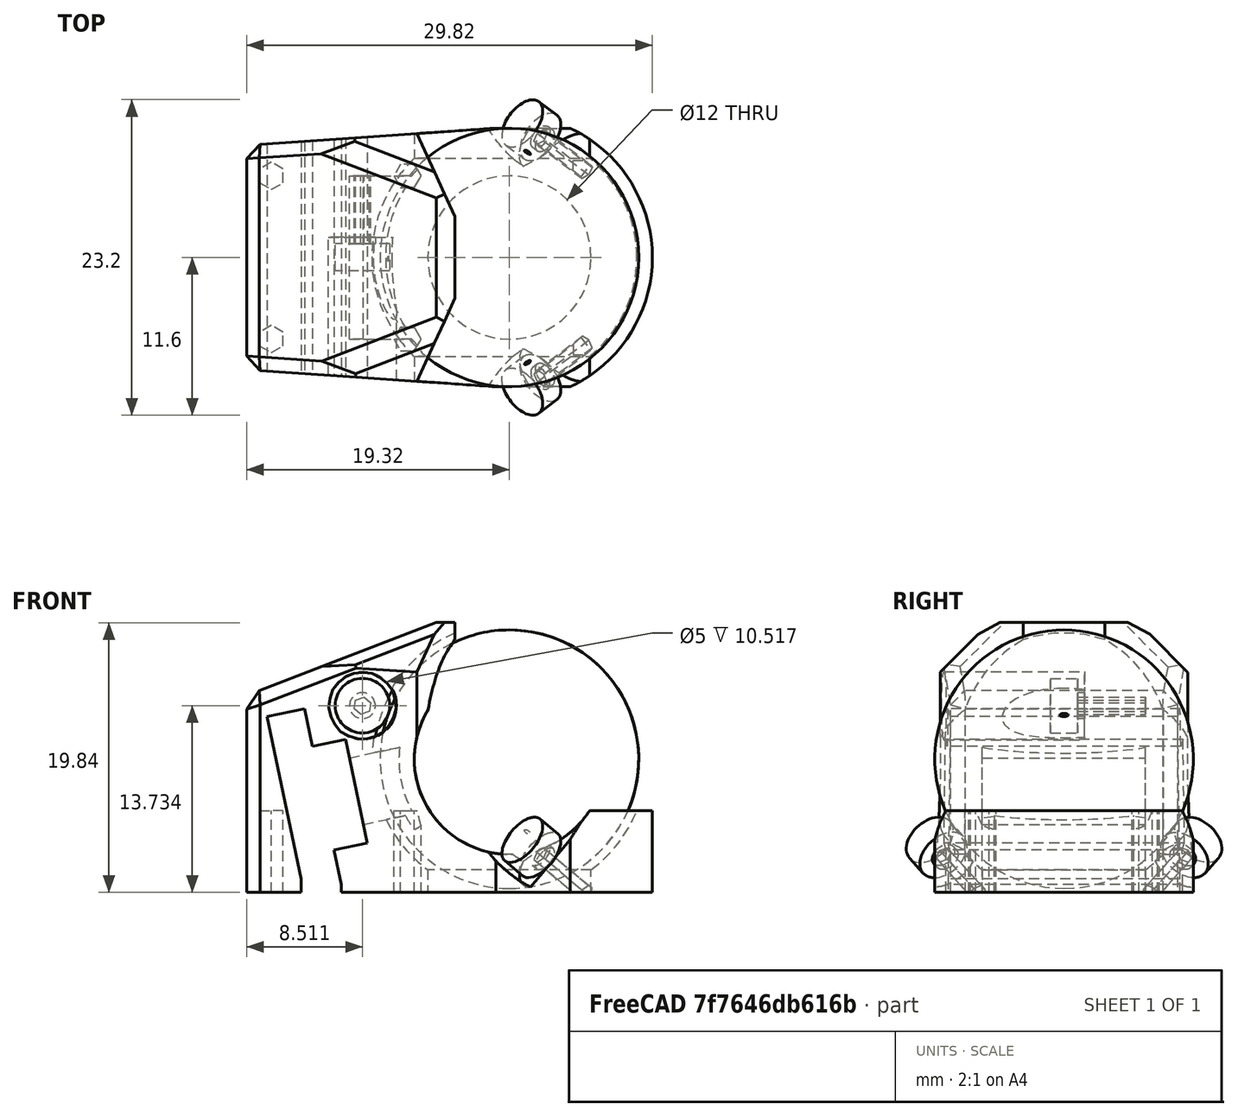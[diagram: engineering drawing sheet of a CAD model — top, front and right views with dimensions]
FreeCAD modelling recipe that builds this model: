
FCSTD DOCUMENT  (FreeCAD 0.21R33771 (Git))
Label: trackball-case-19mm
License: All rights reserved
LicenseURL: http://en.wikipedia.org/wiki/All_rights_reserved
objects: Sketcher::SketchObject×16, PartDesign::Pocket×11, PartDesign::Pad×3, PartDesign::Line×2, PartDesign::PolarPattern×2, PartDesign::Body×2, Spreadsheet::Sheet×1, PartDesign::AdditiveSphere×1, PartDesign::Point×1, PartDesign::Plane×1, PartDesign::SubtractiveSphere×1, PartDesign::Mirrored×1, PartDesign::Chamfer×1
note: 59 computed .brp shape members not serialized (recipe doc carries the construction recipe); baked Part::Feature solids carry a one-line shape summary decoded from their .brp

FEATURE [Sketcher::SketchObject] Sketch
  FullyConstrained = false
  MapMode = 5
  Placement = pos=(0,0,0) rot=(1,0,0;1.5708rad)
  Support = -> [XZ_Plane]
  expr: Constraints[18] = Spreadsheet.radius + 2
  expr: Constraints[1] = Spreadsheet.radius * 2
  expr: Constraints[2] = Spreadsheet.ball_z
  expr: Constraints[35] = 2 * (Spreadsheet.radius + Spreadsheet.clearance)
  expr: Constraints[40] = Spreadsheet.radius * 2 - 0.6
  expr: Constraints[86] = Spreadsheet.radius + Spreadsheet.clearance + 1.2
  expr: Constraints[91] = Spreadsheet.radius + 1
  sketch-geometry (32):
    g0: Circle CenterX=0 CenterY=9.8 CenterZ=0 NormalX=0 NormalY=0 NormalZ=1 AngleXU=0 Radius=9.5025
    g1: LineSegment StartX=0 StartY=9.8 StartZ=0 EndX=-23.9742 EndY=4.78934 EndZ=0
    g2: LineSegment StartX=-12.6299 StartY=14.0051 StartZ=0 EndX=-17.8178 EndY=12.9208 EndZ=0
    g3: LineSegment StartX=-17.8178 StartY=12.9208 StartZ=0 EndX=-15.1173 EndY=0 EndZ=0
    g4: LineSegment StartX=-15.1173 StartY=0 StartZ=0 EndX=-9.92944 EndY=1.08428 EndZ=0
    g5: LineSegment StartX=-9.92944 StartY=1.08428 StartZ=0 EndX=-12.6299 EndY=14.0051 EndZ=0
    g6: LineSegment StartX=-9.92944 StartY=1.08428 StartZ=0 EndX=-11.2592 EndY=7.4468 EndZ=0
    g7: LineSegment StartX=10.5025 StartY=10 StartZ=0 EndX=10.5025 EndY=0 EndZ=0
    g8: LineSegment StartX=10.5025 StartY=6 StartZ=0 EndX=0 EndY=6 EndZ=0
    g9: LineSegment StartX=0 StartY=6 StartZ=0 EndX=-3.31715 EndY=19.3424 EndZ=0
    g10: LineSegment StartX=-3.31715 StartY=19.3424 StartZ=0 EndX=-19.3178 EndY=19.3424 EndZ=0
    g11: LineSegment StartX=-19.3178 StartY=19.3424 StartZ=0 EndX=-19.3178 EndY=0 EndZ=0
    g12: LineSegment StartX=-19.3178 StartY=0 StartZ=0 EndX=10.5025 EndY=0 EndZ=0
    g13: LineSegment StartX=10.5025 StartY=0 StartZ=0 EndX=10.5025 EndY=6 EndZ=0
    g14: Circle CenterX=0 CenterY=9.8 CenterZ=0 NormalX=0 NormalY=0 NormalZ=1 AngleXU=0 Radius=10.1025
    g15: LineSegment StartX=0 StartY=6 StartZ=0 EndX=9.36058 EndY=6 EndZ=0
    g16: LineSegment StartX=-3.44146 StartY=19.8424 StartZ=0 EndX=-3.31715 EndY=19.3424 EndZ=0
    g17: LineSegment StartX=-15.077 StartY=13.4936 StartZ=0 EndX=-17.8178 EndY=12.9208 EndZ=0
    g18: LineSegment StartX=-17.8178 StartY=12.9208 StartZ=0 EndX=-15.3263 EndY=1 EndZ=0
    g19: LineSegment StartX=-15.3263 StartY=1 StartZ=0 EndX=-15.3263 EndY=0 EndZ=0
    g20: LineSegment StartX=-15.3263 StartY=0 StartZ=0 EndX=-19.3178 EndY=0 EndZ=0
    g21: LineSegment StartX=-15.077 StartY=13.4936 StartZ=0 EndX=-14.5042 EndY=10.7529 EndZ=0
    g22: LineSegment StartX=-14.5042 StartY=10.7529 StartZ=0 EndX=-12.0571 EndY=11.2643 EndZ=0
    g23: LineSegment StartX=-12.0571 StartY=11.2643 StartZ=0 EndX=-10.4613 EndY=3.62929 EndZ=0
    g24: LineSegment StartX=-10.4613 StartY=3.62929 StartZ=0 EndX=-12.9085 EndY=3.11784 EndZ=0
    g25: LineSegment StartX=-12.9085 StartY=3.11784 StartZ=0 EndX=-12.3766 EndY=0.572828 EndZ=0
    g26: LineSegment StartX=-12.3766 StartY=0.572828 StartZ=0 EndX=-12.3766 EndY=0 EndZ=0
    g27: LineSegment StartX=-12.3766 StartY=0 StartZ=0 EndX=10.5025 EndY=0 EndZ=0
    g28: LineSegment StartX=-15.077 StartY=13.4936 StartZ=0 EndX=-12.3766 EndY=0.572828 EndZ=0
    g29: LineSegment StartX=-19.3178 StartY=0 StartZ=0 EndX=-19.3178 EndY=14.4871 EndZ=0
    g30: LineSegment StartX=-19.3178 StartY=14.4871 StartZ=0 EndX=-5.37659 EndY=19.8424 EndZ=0
    g31: LineSegment StartX=-5.37659 StartY=19.8424 StartZ=0 EndX=-3.44146 EndY=19.8424 EndZ=0
  constraints (92):
    c: PointOnObject(g0,g-2)
    c: Diameter(g0) = 19.005
    c: Distance(g0,g-1) = 9.8
    c: Coincident(g1,g0)
    c: Coincident(g3,g2)
    c: Coincident(g4,g3)
    c: Coincident(g5,g4)
    c: Coincident(g5,g2)
    c: Perpendicular(g1,g5)
    c: Perpendicular(g1,g3)
    c: Parallel(g2,g1)
    c: Parallel(g4,g1)
    c: Distance(g3,g1) = 6.5
    c: Distance(g2,g1) = 6.7
    c: Distance(g4) = 5.3
    c: Coincident(g6,g4)
    c: PointOnObject(g6,g1)
    c: PointOnObject(g6,g5)
    c: Distance(g6,g0) = 11.5025
    c: PointOnObject(g7,g-1)
    c: Vertical(g7)
    c: PointOnObject(g8,g7)
    c: PointOnObject(g8,g-2)
    c: Horizontal(g8)
    c: Coincident(g9,g8)
    c: Coincident(g10,g9)
    c: Horizontal(g10)
    c: Coincident(g11,g10)
    c: PointOnObject(g11,g-1)
    c: Vertical(g11)
    c: Coincident(g12,g11)
    c: Coincident(g12,g7)
    c: Coincident(g13,g12)
    c: Coincident(g13,g8)
    c: Coincident(g14,g0)
    c: Diameter(g14) = 20.205
    c: PointOnObject(g9,g14)
    c: Coincident(g15,g8)
    c: PointOnObject(g15,g8)
    c: PointOnObject(g15,g14)
    c: Distance(g9,g15) = 18.405
    c: Coincident(g16,g9)
    c: Parallel(g16,g9)
    c: Distance(g2,g11) = 1.5
    c: PointOnObject(g3,g12)
    c: PointOnObject(g17,g2)
    c: Coincident(g17,g2)
    c: Coincident(g18,g17)
    c: PointOnObject(g18,g3)
    c: Coincident(g19,g18)
    c: PointOnObject(g19,g12)
    c: Vertical(g19)
    c: Coincident(g20,g19)
    c: Coincident(g20,g11)
    c: Coincident(g21,g17)
    c: Coincident(g22,g21)
    c: PointOnObject(g22,g5)
    c: Coincident(g23,g22)
    c: PointOnObject(g23,g5)
    c: Coincident(g24,g23)
    c: Coincident(g25,g24)
    c: PointOnObject(g25,g4)
    c: Coincident(g26,g25)
    c: PointOnObject(g26,g12)
    c: Vertical(g26)
    c: Coincident(g27,g26)
    c: Coincident(g27,g13)
    c: Coincident(g28,g17)
    c: Coincident(g28,g25)
    c: PointOnObject(g21,g28)
    c: PointOnObject(g24,g28)
    c: Perpendicular(g22,g21)
    c: Perpendicular(g25,g24)
    c: Distance(g22,g1) = 3.9
    c: Distance(g23,g1) = 3.9
    c: Distance(g22) = 2.5
    c: Perpendicular(g1,g28)
    c: Distance(g19) = 1
    c: Coincident(g29,g20)
    c: PointOnObject(g29,g11)
    c: Coincident(g30,g29)
    c: Coincident(g31,g30)
    c: Coincident(g31,g16)
    c: Horizontal(g31)
    c: Distance(g16,g10) = 0.5
    c: Distance(g17,g30) = 2
    c: Distance(g0,g30) = 11.3025
    c: Distance(g15,g8) = 1.14192
    c: Distance(g16,g27) = 19.8424
    c: Distance(g20,g-2) = 19.3178
    c: Distance(g13) = 6
    c: Distance(g8,g13) = 10.5025
FEATURE [Spreadsheet::Sheet] Spreadsheet
  cells = A1='radius; B1(radius)=9.5025; A2='ball_z; B2(ball_z)=9.8; A3='ball_clearance; B3(clearance)=0.6; A4='bearing_radius; B4(bearing_radius)=2; A5='bearing_t; B5(bearing_t)=2; A6='bearing_a1; B6(bearing_a1)=110; A7='bearing_a2; B7(bearing_a2)=30
FEATURE [PartDesign::Pad] Pad
  Direction = (0,-1,-2e-16)
  Length = 19.005
  Length2 = 10
  Midplane = true
  Placement = pos=(0,0,0) rot=(1,0,0;1.5708rad)
  Profile = -> Sketch
  ReferenceAxis = -> Sketch [N_Axis]
  Type = 0
  expr: Length = Spreadsheet.radius * 2
FEATURE [PartDesign::AdditiveSphere] Sphere001
  Angle1 = -90
  Angle2 = 90
  Angle3 = 360
  AttacherType = Attacher::AttachEngine3D
  AttachmentOffset = pos=(0,0,9.8) rot=(0,0,1;0rad)
  MapMode = 5
  Placement = pos=(0,0,9.8) rot=(0,0,1;0rad)
  Radius = 9.5025
  Support = -> [XY_Plane001]
  expr: .AttachmentOffset.Base.z = Spreadsheet.ball_z
  expr: Radius = Spreadsheet.radius
FEATURE [Sketcher::SketchObject] Sketch001
  FullyConstrained = true
  MapMode = 5
  Placement = pos=(0,0,0) rot=(1,0,0;1.5708rad)
  Support = -> [XZ_Plane]
  expr: Constraints[1] = Spreadsheet.ball_z
  expr: Constraints[2] = 7 * 2
  sketch-geometry (1):
    g0: Circle CenterX=0 CenterY=9.8 CenterZ=0 NormalX=0 NormalY=0 NormalZ=1 AngleXU=0 Radius=7
  constraints (3):
    c: PointOnObject(g0,g-2)
    c: Distance(g0,g-1) = 9.8
    c: Diameter(g0) = 14
FEATURE [Sketcher::SketchObject] Sketch002
  FullyConstrained = true
  MapMode = 5
  Support = -> [XY_Plane]
  sketch-geometry (1):
    g0: Circle CenterX=0 CenterY=0 CenterZ=0 NormalX=0 NormalY=0 NormalZ=1 AngleXU=0 Radius=6
  constraints (2):
    c: Coincident(g0,g-1)
    c: Diameter(g0) = 12
FEATURE [Sketcher::SketchObject] Sketch006
  FullyConstrained = false
  MapMode = 5
  Placement = pos=(0,0,0) rot=(1,0,0;1.5708rad)
  Support = -> [XZ_Plane]
  expr: Constraints[1] = Spreadsheet.ball_z
  expr: Constraints[2] = Spreadsheet.bearing_a1
  expr: Constraints[3] = Spreadsheet.bearing_a2
  expr: Constraints[5] = (Spreadsheet.bearing_a1 + Spreadsheet.bearing_a2) / 2
  sketch-geometry (3):
    g0: LineSegment StartX=0 StartY=9.8 StartZ=0 EndX=-24.3543 EndY=18.6642 EndZ=0
    g1: LineSegment StartX=-0.855559 StartY=12.664 StartZ=0 EndX=7.91392 EndY=-2.52517 EndZ=0
    g2: LineSegment StartX=7.70104 StartY=18.9777 StartZ=0 EndX=-6.79818 EndY=1.69825 EndZ=0
  constraints (6):
    c: PointOnObject(g0,g-2)
    c: Distance(g0,g-1) = 9.8
    c: Angle(g0,g-2) = 1.91986
    c: Angle(g-2,g1) = 0.523599
    c: PointOnObject(g0,g2)
    c: Angle(g0,g2) = 1.22173
FEATURE [PartDesign::Line] DatumLine
  AttacherType = Attacher::AttachEngineLine
  Length = 20
  MapMode = 29
  Placement = pos=(-4.82556,-9e-16,4.04912) rot=(-0.684791,0.684791,0.249244;3.63013rad)
  ResizeMode = 0
  Support = -> [Sketch006]
FEATURE [PartDesign::Point] DatumPoint
  AttacherType = Attacher::AttachEnginePoint
  AttachmentOffset = pos=(0,0,9.8) rot=(0,0,1;0rad)
  MapMode = 41
  Placement = pos=(0,0,9.8) rot=(0,0,1;0rad)
  Support = -> [X_Axis,Y_Axis]
  expr: .AttachmentOffset.Base.z = Spreadsheet.ball_z
FEATURE [PartDesign::Plane] DatumPlane
  AttachmentOffset = pos=(0,0,0) rot=(0.654654,0.377964,-0.654654;2.41886rad)
  Length = 85.316
  MapMode = 7
  Placement = pos=(1.8e-15,-3.4e-15,9.8) rot=(0.11982,0.958967,-0.256954;2.30059rad)
  ResizeMode = 0
  Support = -> [DatumLine,DatumPoint]
  Width = 93.3965
FEATURE [Sketcher::SketchObject] Sketch003
  FullyConstrained = true
  MapMode = 5
  Placement = pos=(9e-16,-3.6e-15,9.8) rot=(0.11982,0.958967,-0.256954;2.30059rad)
  Support = -> [DatumPlane]
  expr: Constraints[0] = Spreadsheet.bearing_radius * 2
  expr: Constraints[2] = Spreadsheet.radius + Spreadsheet.bearing_radius
  expr: Constraints[4] = (Spreadsheet.bearing_radius + 0.5) * 2
  expr: Constraints[6] = (Spreadsheet.bearing_a1 + Spreadsheet.bearing_a2) / 2
  sketch-geometry (3):
    g0: Circle CenterX=3.93409 CenterY=10.8088 CenterZ=0 NormalX=0 NormalY=0 NormalZ=1 AngleXU=0 Radius=2
    g1: LineSegment StartX=0 StartY=0 StartZ=0 EndX=3.93409 EndY=10.8088 EndZ=0
    g2: Circle CenterX=3.93409 CenterY=10.8088 CenterZ=0 NormalX=0 NormalY=0 NormalZ=1 AngleXU=0 Radius=2.5
  constraints (7):
    c: Diameter(g0) = 4
    c: Coincident(g1,g0)
    c: Distance(g1) = 11.5025
    c: Coincident(g2,g0)
    c: Diameter(g2) = 5
    c: Coincident(g1,g-1)
    c: Angle(g-1,g1) = 1.22173
FEATURE [Sketcher::SketchObject] Sketch004
  AttachmentOffset = pos=(0,0,1) rot=(0,0,1;0rad)
  FullyConstrained = true
  MapMode = 5
  Placement = pos=(0.663414,-0.5,9.24333) rot=(0.11982,0.958967,-0.256954;2.30059rad)
  Support = -> [DatumPlane]
  expr: .AttachmentOffset.Base.z = Spreadsheet.bearing_t / 2
  expr: Constraints[0] = Spreadsheet.bearing_radius * 2
  expr: Constraints[2] = Spreadsheet.radius + Spreadsheet.bearing_radius
  expr: Constraints[6] = (Spreadsheet.bearing_a1 + Spreadsheet.bearing_a2) / 2
  sketch-geometry (3):
    g0: Circle CenterX=3.93409 CenterY=10.8088 CenterZ=0 NormalX=0 NormalY=0 NormalZ=1 AngleXU=0 Radius=2
    g1: LineSegment StartX=0 StartY=0 StartZ=0 EndX=3.93409 EndY=10.8088 EndZ=0
    g2: Circle CenterX=3.93409 CenterY=10.8088 CenterZ=0 NormalX=0 NormalY=0 NormalZ=1 AngleXU=0 Radius=0.95
  constraints (7):
    c: Diameter(g0) = 4
    c: Coincident(g1,g0)
    c: Distance(g1) = 11.5025
    c: Coincident(g2,g0)
    c: Diameter(g2) = 1.9
    c: Coincident(g1,g-1)
    c: Angle(g-1,g1) = 1.22173
FEATURE [Sketcher::SketchObject] Sketch005
  AttachmentOffset = pos=(0,0,1) rot=(0,0,1;0rad)
  FullyConstrained = true
  MapMode = 5
  Placement = pos=(0.663414,-0.5,9.24333) rot=(0.11982,0.958967,-0.256954;2.30059rad)
  Support = -> [DatumPlane]
  expr: .AttachmentOffset.Base.z = Spreadsheet.bearing_t / 2
  expr: Constraints[0] = Spreadsheet.bearing_radius * 2
  expr: Constraints[29] = (Spreadsheet.bearing_a1 + Spreadsheet.bearing_a2) / 2
  expr: Constraints[2] = Spreadsheet.radius + Spreadsheet.bearing_radius
  sketch-geometry (11):
    g0: Circle CenterX=3.93409 CenterY=10.8088 CenterZ=0 NormalX=0 NormalY=0 NormalZ=1 AngleXU=0 Radius=2
    g1: LineSegment StartX=0 StartY=0 StartZ=0 EndX=3.93409 EndY=10.8088 EndZ=0
    g2: LineSegment StartX=3.93409 StartY=10.8088 StartZ=0 EndX=3.93409 EndY=12.8088 EndZ=0
    g3: Circle CenterX=3.93409 CenterY=10.8088 CenterZ=0 NormalX=0 NormalY=0 NormalZ=1 AngleXU=0 Radius=0.65
    g4: LineSegment StartX=3.93409 StartY=11.4588 StartZ=0 EndX=3.37117 EndY=11.1338 EndZ=0
    g5: LineSegment StartX=3.37117 StartY=11.1338 StartZ=0 EndX=3.37117 EndY=10.4838 EndZ=0
    g6: LineSegment StartX=3.37117 StartY=10.4838 StartZ=0 EndX=3.93409 EndY=10.1588 EndZ=0
    g7: LineSegment StartX=3.93409 StartY=10.1588 StartZ=0 EndX=4.497 EndY=10.4838 EndZ=0
    g8: LineSegment StartX=4.497 StartY=10.4838 StartZ=0 EndX=4.497 EndY=11.1338 EndZ=0
    g9: LineSegment StartX=4.497 StartY=11.1338 StartZ=0 EndX=3.93409 EndY=11.4588 EndZ=0
    g10: Circle CenterX=3.93409 CenterY=10.8088 CenterZ=0 NormalX=0 NormalY=0 NormalZ=1 AngleXU=0 Radius=0.65
  constraints (26):
    c: Diameter(g0) = 4
    c: Coincident(g1,g0)
    c: Distance(g1) = 11.5025
    c: Coincident(g2,g0)
    c: PointOnObject(g2,g0)
    c: Vertical(g2)
    c: Coincident(g3,g0)
    c: Diameter(g3) = 1.3
    c: Coincident(g4,g5)
    c: Coincident(g5,g6)
    c: Coincident(g6,g7)
    c: Coincident(g7,g8)
    c: Coincident(g8,g9)
    c: Coincident(g9,g4)
    c: Equal(g4, g5-g9) x5
    c: PointOnObject(g4,g10)
    c: PointOnObject(g5,g10)
    c: PointOnObject(g6,g10)
    c: PointOnObject(g7,g10)
    c: PointOnObject(g8,g10)
    c: PointOnObject(g9,g10)
    c: Coincident(g10,g0)
    c: PointOnObject(g9,g3)
    c: PointOnObject(g4,g2)
    c: Coincident(g1,g-1)
    c: Angle(g-1,g1) = 1.22173
FEATURE [Sketcher::SketchObject] Sketch007
  FullyConstrained = true
  MapMode = 5
  Support = -> [XY_Plane]
  expr: Constraints[6] = Spreadsheet.radius + 1
  expr: Constraints[7] = Spreadsheet.radius * 2
  sketch-geometry (4):
    g0: ArcOfCircle CenterX=0 CenterY=0 CenterZ=0 NormalX=0 NormalY=0 NormalZ=1 AngleXU=0 Radius=10.5025 StartAngle=4.71239 EndAngle=7.85398
    g1: ArcOfCircle CenterX=0 CenterY=0 CenterZ=0 NormalX=0 NormalY=0 NormalZ=1 AngleXU=0 Radius=19.005 StartAngle=4.71239 EndAngle=7.85398
    g2: LineSegment StartX=0 StartY=19.005 StartZ=0 EndX=0 EndY=10.5025 EndZ=0
    g3: LineSegment StartX=0 StartY=-10.5025 StartZ=0 EndX=-3.5e-15 EndY=-19.005 EndZ=0
  constraints (12):
    c: Coincident(g0,g-1)
    c: PointOnObject(g0,g-2)
    c: PointOnObject(g0,g-2)
    c: Coincident(g1,g0)
    c: PointOnObject(g1,g-2)
    c: PointOnObject(g1,g-2)
    c: Radius(g0) = 10.5025
    c: Radius(g1) = 19.005
    c: Coincident(g2,g1)
    c: Coincident(g2,g0)
    c: Coincident(g3,g0)
    c: Coincident(g3,g1)
FEATURE [Sketcher::SketchObject] Sketch008
  FullyConstrained = true
  MapMode = 5
  Support = -> [XY_Plane]
  expr: Constraints[10] = Spreadsheet.radius * 2
  expr: Constraints[33] = Spreadsheet.radius * 2
  expr: Constraints[34] = Spreadsheet.radius * 2
  expr: Constraints[36] = Spreadsheet.radius * 2
  sketch-geometry (14):
    g0: LineSegment StartX=-23 StartY=-9.5025 StartZ=0 EndX=-23 EndY=9.5025 EndZ=0
    g1: LineSegment StartX=-23 StartY=9.5025 StartZ=0 EndX=0 EndY=9.5025 EndZ=0
    g2: LineSegment StartX=0 StartY=9.5025 StartZ=0 EndX=0 EndY=-9.5025 EndZ=0
    g3: LineSegment StartX=0 StartY=-9.5025 StartZ=0 EndX=-23 EndY=-9.5025 EndZ=0
    g4: GeomPoint X=-11.5 Y=0 Z=0
    g5: LineSegment StartX=-23 StartY=8 StartZ=0 EndX=-1 EndY=9.5025 EndZ=0
    g6: LineSegment StartX=-1 StartY=9.5025 StartZ=0 EndX=-1 EndY=-9.5025 EndZ=0
    g7: LineSegment StartX=-1 StartY=-9.5025 StartZ=0 EndX=-23 EndY=-8 EndZ=0
    g8: LineSegment StartX=-1 StartY=-9.5025 StartZ=0 EndX=-1 EndY=-19.005 EndZ=0
    g9: LineSegment StartX=-1 StartY=-19.005 StartZ=0 EndX=-20.005 EndY=-19.005 EndZ=0
    g10: LineSegment StartX=-20.005 StartY=-19.005 StartZ=0 EndX=-20.005 EndY=19.005 EndZ=0
    g11: LineSegment StartX=-20.005 StartY=19.005 StartZ=0 EndX=-1 EndY=19.005 EndZ=0
    g12: LineSegment StartX=-1 StartY=19.005 StartZ=0 EndX=-1 EndY=9.5025 EndZ=0
    g13: LineSegment StartX=-23 StartY=8 StartZ=0 EndX=-23 EndY=-8 EndZ=0
  constraints (39):
    c: Coincident(g0,g1)
    c: Coincident(g1,g2)
    c: Coincident(g2,g3)
    c: Coincident(g3,g0)
    c: Horizontal(g1)
    c: Horizontal(g3)
    c: Vertical(g0)
    c: Vertical(g2)
    c: Symmetric(g1,g0,g4)
    c: PointOnObject(g4,g-1)
    c: Distance(g0) = 19.005
    c: PointOnObject(g1,g-2)
    c: Distance(g-1,g0) = 23
    c: PointOnObject(g5,g0)
    c: PointOnObject(g5,g1)
    c: Coincident(g6,g5)
    c: PointOnObject(g6,g3)
    c: Vertical(g6)
    c: Coincident(g7,g6)
    c: PointOnObject(g7,g0)
    c: Distance(g5,g-1) = 8
    c: Distance(g7,g-1) = 8
    c: Coincident(g8,g7)
    c: Vertical(g8)
    c: Coincident(g9,g8)
    c: Horizontal(g9)
    c: Coincident(g10,g9)
    c: Vertical(g10)
    c: Coincident(g11,g10)
    c: Horizontal(g11)
    c: Coincident(g12,g11)
    c: Coincident(g12,g5)
    c: Vertical(g12)
    c: Distance(g10,g-1) = 19.005
    c: Distance(g9,g-1) = 19.005
    c: Distance(g7,g-2) = 1
    c: Distance(g9) = 19.005
    c: Coincident(g13,g5)
    c: Coincident(g13,g7)
FEATURE [Sketcher::SketchObject] Sketch009
  FullyConstrained = false
  MapMode = 5
  Placement = pos=(0,0,0) rot=(1,0,0;1.5708rad)
  Support = -> [XZ_Plane]
  expr: Constraints[18] = Spreadsheet.radius + 2
  expr: Constraints[1] = Spreadsheet.radius * 2
  expr: Constraints[24] = 2 * (Spreadsheet.radius + Spreadsheet.clearance)
  expr: Constraints[2] = Spreadsheet.ball_z
  expr: Constraints[37] = Spreadsheet.radius + 3
  sketch-geometry (14):
    g0: Circle CenterX=0 CenterY=9.8 CenterZ=0 NormalX=0 NormalY=0 NormalZ=1 AngleXU=0 Radius=9.5025
    g1: LineSegment StartX=0 StartY=9.8 StartZ=0 EndX=-24.0621 EndY=4.77097 EndZ=0
    g2: LineSegment StartX=-12.6299 StartY=14.0051 StartZ=0 EndX=-17.8178 EndY=12.9208 EndZ=0
    g3: LineSegment StartX=-17.8178 StartY=12.9208 StartZ=0 EndX=-15.1173 EndY=0 EndZ=0
    g4: LineSegment StartX=-15.1173 StartY=0 StartZ=0 EndX=-9.92944 EndY=1.08428 EndZ=0
    g5: LineSegment StartX=-9.92944 StartY=1.08428 StartZ=0 EndX=-12.6299 EndY=14.0051 EndZ=0
    g6: LineSegment StartX=-9.92944 StartY=1.08428 StartZ=0 EndX=-11.2592 EndY=7.4468 EndZ=0
    g7: LineSegment StartX=-4.65284 StartY=18.7672 StartZ=0 EndX=-19.0178 EndY=18.7672 EndZ=0
    g8: LineSegment StartX=-19.0178 StartY=18.7672 StartZ=0 EndX=-19.0178 EndY=0 EndZ=0
    g9: Circle CenterX=0 CenterY=9.8 CenterZ=0 NormalX=0 NormalY=0 NormalZ=1 AngleXU=0 Radius=10.1025
    g10: LineSegment StartX=-12.7495 StartY=9.68935 StartZ=0 EndX=-11.7266 EndY=4.7951 EndZ=0
    g11: LineSegment StartX=-11.7266 StartY=4.7951 StartZ=0 EndX=0.511453 EndY=7.35288 EndZ=0
    g12: LineSegment StartX=-12.7495 StartY=9.68935 StartZ=0 EndX=-0.511453 EndY=12.2471 EndZ=0
    g13: LineSegment StartX=-0.511453 StartY=12.2471 StartZ=0 EndX=0.511453 EndY=7.35288 EndZ=0
  constraints (40):
    c: PointOnObject(g0,g-2)
    c: Diameter(g0) = 19.005
    c: Distance(g0,g-1) = 9.8
    c: Coincident(g1,g0)
    c: Coincident(g3,g2)
    c: Coincident(g4,g3)
    c: Coincident(g5,g4)
    c: Coincident(g5,g2)
    c: Perpendicular(g1,g5)
    c: Perpendicular(g1,g3)
    c: Parallel(g2,g1)
    c: Parallel(g4,g1)
    c: Distance(g3,g1) = 6.5
    c: Distance(g2,g1) = 6.7
    c: Distance(g4) = 5.3
    c: Coincident(g6,g4)
    c: PointOnObject(g6,g1)
    c: PointOnObject(g6,g5)
    c: Distance(g6,g0) = 11.5025
    c: Horizontal(g7)
    c: Coincident(g8,g7)
    c: PointOnObject(g8,g-1)
    c: Vertical(g8)
    c: Coincident(g9,g0)
    c: Diameter(g9) = 20.205
    c: PointOnObject(g7,g9)
    c: Distance(g2,g8) = 1.2
    c: PointOnObject(g3,g-1)
    c: Coincident(g11,g10)
    c: Coincident(g12,g10)
    c: Coincident(g13,g12)
    c: Coincident(g13,g11)
    c: Perpendicular(g1,g10)
    c: Perpendicular(g1,g13)
    c: Perpendicular(g13,g11)
    c: Perpendicular(g13,g12)
    c: PointOnObject(g0,g13)
    c: Distance(g0,g10) = 12.5025
    c: Distance(g10,g1) = 2.5
    c: Distance(g10,g1) = 2.5
FEATURE [PartDesign::Pocket] Pocket006  label="センサービューポート"
  BaseFeature = -> Pad
  Direction = (0,1,2e-16)
  Length = 12
  Length2 = 5
  Midplane = true
  Placement = pos=(0,0,0) rot=(1,0,0;1.5708rad)
  Profile = -> Sketch009
  ReferenceAxis = -> Sketch009 [N_Axis]
  Type = 0
FEATURE [PartDesign::SubtractiveSphere] Sphere
  Angle1 = -90
  Angle2 = 90
  Angle3 = 360
  AttacherType = Attacher::AttachEngine3D
  AttachmentOffset = pos=(0,0,9.8) rot=(0,0,1;0rad)
  BaseFeature = -> Pocket006
  MapMode = 5
  Placement = pos=(0,0,9.8) rot=(0,0,1;0rad)
  Radius = 10.1025
  Support = -> [XY_Plane]
  expr: .AttachmentOffset.Base.z = Spreadsheet.ball_z
  expr: Radius = Spreadsheet.radius + Spreadsheet.clearance
FEATURE [PartDesign::Pocket] Pocket  label="側面穴"
  BaseFeature = -> Sphere
  Direction = (0,1,2e-16)
  Length = 100
  Length2 = 5
  Midplane = true
  Placement = pos=(0,0,9.8) rot=(0,0,1;0rad)
  Profile = -> Sketch001
  ReferenceAxis = -> Sketch001 [N_Axis]
  Type = 0
FEATURE [PartDesign::Pocket] Pocket001  label="底面穴"
  BaseFeature = -> Pocket
  Direction = (0,0,-1)
  Length = 9.5025
  Length2 = 5
  Placement = pos=(0,0,9.8) rot=(0,0,1;0rad)
  Profile = -> Sketch002
  ReferenceAxis = -> Sketch002 [N_Axis]
  Reversed = true
  Type = 0
  expr: Length = Spreadsheet.radius
FEATURE [Sketcher::SketchObject] Sketch010
  FullyConstrained = true
  MapMode = 5
  Placement = pos=(9e-16,-3.6e-15,9.8) rot=(0.11982,0.958967,-0.256954;2.30059rad)
  Support = -> [DatumPlane]
  expr: Constraints[0] = Spreadsheet.bearing_radius * 2
  expr: Constraints[2] = Spreadsheet.radius + Spreadsheet.bearing_radius
  expr: Constraints[4] = (Spreadsheet.bearing_radius + 0.5) * 2
  expr: Constraints[6] = (Spreadsheet.bearing_a1 + Spreadsheet.bearing_a2) / 2
  sketch-geometry (7):
    g0: Circle CenterX=3.93409 CenterY=10.8088 CenterZ=0 NormalX=0 NormalY=0 NormalZ=1 AngleXU=0 Radius=2
    g1: LineSegment StartX=0 StartY=0 StartZ=0 EndX=3.93409 EndY=10.8088 EndZ=0
    g2: Circle CenterX=3.93409 CenterY=10.8088 CenterZ=0 NormalX=0 NormalY=0 NormalZ=1 AngleXU=0 Radius=2.5
    g3: LineSegment StartX=4.78914 StartY=13.158 StartZ=0 EndX=3.07904 EndY=8.45958 EndZ=0
    g4: LineSegment StartX=3.07904 StartY=8.45958 StartZ=0 EndX=-6.31788 EndY=11.8798 EndZ=0
    g5: LineSegment StartX=4.78914 StartY=13.158 StartZ=0 EndX=-4.6078 EndY=16.5782 EndZ=0
    g6: LineSegment StartX=-4.6078 StartY=16.5782 StartZ=0 EndX=-6.31788 EndY=11.8798 EndZ=0
  constraints (19):
    c: Diameter(g0) = 4
    c: Coincident(g1,g0)
    c: Distance(g1) = 11.5025
    c: Coincident(g2,g0)
    c: Diameter(g2) = 5
    c: Coincident(g1,g-1)
    c: Angle(g-1,g1) = 1.22173
    c: PointOnObject(g3,g2)
    c: PointOnObject(g3,g2)
    c: PointOnObject(g0,g3)
    c: PointOnObject(g3,g1)
    c: Coincident(g4,g3)
    c: Tangent(g4,g2)
    c: Coincident(g5,g3)
    c: Tangent(g5,g2)
    c: Coincident(g6,g5)
    c: Coincident(g6,g4)
    c: Parallel(g6,g3)
    c: Distance(g5) = 10
FEATURE [PartDesign::Pocket] Pocket007  label="ベアリング切り欠き1"
  BaseFeature = -> Pocket001
  Direction = (-0.663414,0.5,0.55667)
  Length = 5
  Length2 = 1.5
  Placement = pos=(0,0,9.8) rot=(0,0,1;0rad)
  Profile = -> Sketch010
  ReferenceAxis = -> Sketch010 [N_Axis]
  Type = 4
  expr: Length2 = Spreadsheet.bearing_t / 2 + 0.5
FEATURE [PartDesign::Pocket] Pocket002  label="ベアリング切り欠き2"
  BaseFeature = -> Pocket007
  Direction = (-0.663414,0.5,0.55667)
  Length = 1.5
  Length2 = 9.5025
  Placement = pos=(0,0,9.8) rot=(0,0,1;0rad)
  Profile = -> Sketch003
  ReferenceAxis = -> Sketch003 [N_Axis]
  Reversed = true
  Type = 4
  expr: Length = Spreadsheet.bearing_t / 2 + 0.5
  expr: Length2 = Spreadsheet.radius
FEATURE [PartDesign::Pad] Pad001  label="ベアリングネジ固定台座"
  BaseFeature = -> Pocket002
  Direction = (0.663414,-0.5,-0.55667)
  Length = 2
  Length2 = 10
  Placement = pos=(0,0,9.8) rot=(0,0,1;0rad)
  Profile = -> Sketch004
  ReferenceAxis = -> Sketch004 [N_Axis]
  Type = 0
  expr: Length = Spreadsheet.bearing_t
FEATURE [PartDesign::Pocket] Pocket003  label="ベアリング固定ネジ穴"
  BaseFeature = -> Pad001
  Direction = (-0.663414,0.5,0.55667)
  Length = 5
  Length2 = 5
  Placement = pos=(0,0,9.8) rot=(0,0,1;0rad)
  Profile = -> Sketch005
  ReferenceAxis = -> Sketch005 [N_Axis]
  Reversed = true
  Type = 0
FEATURE [PartDesign::PolarPattern] PolarPattern
  Angle = 120
  Axis = -> DatumLine
  BaseFeature = -> Pocket003
  Occurrences = 2
  Originals = -> [Pocket002,Pad001,Pocket003]
  Placement = pos=(0,0,9.8) rot=(0,0,1;0rad)
  Reversed = true
FEATURE [PartDesign::Mirrored] Mirrored
  BaseFeature = -> PolarPattern
  MirrorPlane = -> XZ_Plane
  Originals = -> [Pocket007,Pocket002,Pad001,Pocket003]
  Placement = pos=(0,0,9.8) rot=(0,0,1;0rad)
FEATURE [PartDesign::Pocket] Pocket004  label="外形カット1"
  BaseFeature = -> Mirrored
  Direction = (0,0,-1)
  Length = 9.5025
  Length2 = 5
  Placement = pos=(0,0,9.8) rot=(0,0,1;0rad)
  Profile = -> Sketch007
  ReferenceAxis = -> Sketch007 [N_Axis]
  Reversed = true
  Type = 0
  expr: Length = Spreadsheet.radius
FEATURE [PartDesign::Pocket] Pocket005  label="外形カット2"
  BaseFeature = -> Pocket004
  Direction = (0,0,-1)
  Length = 28.5075
  Length2 = 5
  Placement = pos=(0,0,9.8) rot=(0,0,1;0rad)
  Profile = -> Sketch008
  ReferenceAxis = -> Sketch008 [N_Axis]
  Reversed = true
  Type = 0
  expr: Length = Spreadsheet.radius * 3
FEATURE [Sketcher::SketchObject] Sketch011
  AttachmentOffset = pos=(0,0,9.8) rot=(0,0,1;0rad)
  FullyConstrained = true
  MapMode = 5
  Placement = pos=(0,0,9.8) rot=(0,0,1;0rad)
  Support = -> [XY_Plane]
  expr: .AttachmentOffset.Base.z = Spreadsheet.ball_z
  expr: Constraints[24] = Spreadsheet.radius
  sketch-geometry (9):
    g0: LineSegment StartX=-4 StartY=-3 StartZ=0 EndX=-9.07497 EndY=-14 EndZ=0
    g1: LineSegment StartX=-9.07497 StartY=-14 StartZ=0 EndX=0 EndY=-14 EndZ=0
    g2: LineSegment StartX=0 StartY=-14 StartZ=0 EndX=0 EndY=14 EndZ=0
    g3: LineSegment StartX=-9.07497 StartY=-14 StartZ=0 EndX=-9.07497 EndY=14 EndZ=0
    g4: LineSegment StartX=-4 StartY=-3 StartZ=0 EndX=-4 EndY=3 EndZ=0
    g5: LineSegment StartX=0 StartY=14 StartZ=0 EndX=-9.07497 EndY=14 EndZ=0
    g6: LineSegment StartX=-9.07497 StartY=14 StartZ=0 EndX=-4 EndY=3 EndZ=0
    g7: LineSegment StartX=-4 StartY=3 StartZ=0 EndX=-4 EndY=-3 EndZ=0
    g8: LineSegment StartX=-7 StartY=-9.5025 StartZ=0 EndX=0 EndY=-9.5025 EndZ=0
  constraints (26):
    c: Coincident(g1,g0)
    c: Horizontal(g1)
    c: Coincident(g2,g1)
    c: Vertical(g2)
    c: Coincident(g3,g0)
    c: Vertical(g3)
    c: Coincident(g4,g0)
    c: Vertical(g4)
    c: Coincident(g5,g2)
    c: Coincident(g5,g3)
    c: Horizontal(g5)
    c: Coincident(g6,g5)
    c: Coincident(g6,g4)
    c: Coincident(g7,g6)
    c: Coincident(g7,g0)
    c: Distance(g-1,g7) = 4
    c: Distance(g-1,g5) = 14
    c: Distance(g-1,g1) = 14
    c: PointOnObject(g-1,g2)
    c: Distance(g0,g-1) = 3
    c: Distance(g6,g-1) = 3
    c: PointOnObject(g8,g0)
    c: PointOnObject(g8,g2)
    c: Horizontal(g8)
    c: Distance(g-1,g8) = 9.5025
    c: Distance(g8) = 7
FEATURE [PartDesign::Pocket] Pocket008  label="外形カット3"
  BaseFeature = -> Pocket005
  Direction = (0,0,-1)
  Length = 19.005
  Length2 = 5
  Placement = pos=(0,0,9.8) rot=(0,0,1;0rad)
  Profile = -> Sketch011
  ReferenceAxis = -> Sketch011 [N_Axis]
  Reversed = true
  Type = 0
  expr: Length = Spreadsheet.radius * 2
FEATURE [Sketcher::SketchObject] Sketch012
  FullyConstrained = true
  MapMode = 5
  Placement = pos=(0,0,0) rot=(0.57735,0.57735,0.57735;2.0944rad)
  Support = -> [YZ_Plane]
  expr: Constraints[13] = Spreadsheet.ball_z + Spreadsheet.radius + 1
  sketch-geometry (7):
    g0: LineSegment StartX=-5 StartY=20.3025 StartZ=0 EndX=-15 EndY=10.3025 EndZ=0
    g1: LineSegment StartX=-15 StartY=10.3025 StartZ=0 EndX=-15 EndY=25.3025 EndZ=0
    g2: LineSegment StartX=-15 StartY=25.3025 StartZ=0 EndX=14.97 EndY=25.3025 EndZ=0
    g3: LineSegment StartX=14.97 StartY=25.3025 StartZ=0 EndX=14.97 EndY=10.3025 EndZ=0
    g4: LineSegment StartX=-15 StartY=10.3025 StartZ=0 EndX=14.97 EndY=10.3025 EndZ=0
    g5: LineSegment StartX=-5 StartY=20.3025 StartZ=0 EndX=4.97 EndY=20.3025 EndZ=0
    g6: LineSegment StartX=4.97 StartY=20.3025 StartZ=0 EndX=14.97 EndY=10.3025 EndZ=0
  constraints (20):
    c: Coincident(g1,g0)
    c: Vertical(g1)
    c: Coincident(g2,g1)
    c: Horizontal(g2)
    c: Coincident(g3,g2)
    c: Vertical(g3)
    c: Coincident(g4,g0)
    c: Coincident(g4,g3)
    c: Horizontal(g4)
    c: Coincident(g5,g0)
    c: Horizontal(g5)
    c: Coincident(g6,g5)
    c: Coincident(g6,g3)
    c: Distance(g-1,g5) = 20.3025
    c: Angle(g6,g4) = 0.785398
    c: Distance(g5,g-2) = 4.97
    c: Distance(g0,g-2) = 5
    c: Distance(g5,g4) = 10
    c: Angle(g4,g0) = 0.785398
    c: Distance(g3) = 15
FEATURE [PartDesign::Pocket] Pocket009  label="外形カット4"
  BaseFeature = -> Pocket008
  Direction = (-1,2e-16,-3e-16)
  Length = 50
  Length2 = 5
  Placement = pos=(0,0,9.8) rot=(0,0,1;0rad)
  Profile = -> Sketch012
  ReferenceAxis = -> Sketch012 [N_Axis]
  Type = 0
FEATURE [Sketcher::SketchObject] Sketch013
  FullyConstrained = true
  MapMode = 5
  Support = -> [XY_Plane]
  expr: Constraints[61] = Spreadsheet.radius + 8
  sketch-geometry (37):
    g0: LineSegment StartX=-7.5 StartY=6 StartZ=0 EndX=7.5 EndY=6 EndZ=0
    g1: LineSegment StartX=7.5 StartY=6 StartZ=0 EndX=7.5 EndY=-6 EndZ=0
    g2: LineSegment StartX=7.5 StartY=-6 StartZ=0 EndX=-7.5 EndY=-6 EndZ=0
    g3: LineSegment StartX=-7.5 StartY=-6 StartZ=0 EndX=-7.5 EndY=6 EndZ=0
    g4: Circle CenterX=-7.5 CenterY=-6 CenterZ=0 NormalX=0 NormalY=0 NormalZ=1 AngleXU=0 Radius=1
    g5: Circle CenterX=-7.5 CenterY=6 CenterZ=0 NormalX=0 NormalY=0 NormalZ=1 AngleXU=0 Radius=1
    g6: LineSegment StartX=-8 StartY=-5.13397 StartZ=0 EndX=-8.5 EndY=-6 EndZ=0
    g7: LineSegment StartX=-8.5 StartY=-6 StartZ=0 EndX=-8 EndY=-6.86603 EndZ=0
    g8: LineSegment StartX=-8 StartY=-6.86603 StartZ=0 EndX=-7 EndY=-6.86603 EndZ=0
    g9: LineSegment StartX=-7 StartY=-6.86603 StartZ=0 EndX=-6.5 EndY=-6 EndZ=0
    g10: LineSegment StartX=-6.5 StartY=-6 StartZ=0 EndX=-7 EndY=-5.13397 EndZ=0
    g11: LineSegment StartX=-7 StartY=-5.13397 StartZ=0 EndX=-8 EndY=-5.13397 EndZ=0
    g12: Circle CenterX=-7.5 CenterY=-6 CenterZ=0 NormalX=0 NormalY=0 NormalZ=1 AngleXU=0 Radius=1
    g13: LineSegment StartX=-8.5 StartY=6 StartZ=0 EndX=-8 EndY=5.13397 EndZ=0
    g14: LineSegment StartX=-8 StartY=5.13397 StartZ=0 EndX=-7 EndY=5.13397 EndZ=0
    g15: LineSegment StartX=-7 StartY=5.13397 StartZ=0 EndX=-6.5 EndY=6 EndZ=0
    g16: LineSegment StartX=-6.5 StartY=6 StartZ=0 EndX=-7 EndY=6.86603 EndZ=0
    g17: LineSegment StartX=-7 StartY=6.86603 StartZ=0 EndX=-8 EndY=6.86603 EndZ=0
    g18: LineSegment StartX=-8 StartY=6.86603 StartZ=0 EndX=-8.5 EndY=6 EndZ=0
    g19: Circle CenterX=-7.5 CenterY=6 CenterZ=0 NormalX=0 NormalY=0 NormalZ=1 AngleXU=0 Radius=1
    g20: LineSegment StartX=-7.5 StartY=6 StartZ=0 EndX=-17.5025 EndY=6 EndZ=0
    g21: LineSegment StartX=-17.5025 StartY=6 StartZ=0 EndX=-17.5025 EndY=-6 EndZ=0
    g22: LineSegment StartX=-17.5025 StartY=-6 StartZ=0 EndX=-7.5 EndY=-6 EndZ=0
    g23: LineSegment StartX=-17.5025 StartY=5 StartZ=0 EndX=-16.6365 EndY=5.5 EndZ=0
    g24: LineSegment StartX=-16.6365 StartY=5.5 StartZ=0 EndX=-16.6365 EndY=6.5 EndZ=0
    g25: LineSegment StartX=-16.6365 StartY=6.5 StartZ=0 EndX=-17.5025 EndY=7 EndZ=0
    g26: LineSegment StartX=-17.5025 StartY=7 StartZ=0 EndX=-18.3685 EndY=6.5 EndZ=0
    g27: LineSegment StartX=-18.3685 StartY=6.5 StartZ=0 EndX=-18.3685 EndY=5.5 EndZ=0
    g28: LineSegment StartX=-18.3685 StartY=5.5 StartZ=0 EndX=-17.5025 EndY=5 EndZ=0
    g29: Circle CenterX=-17.5025 CenterY=6 CenterZ=0 NormalX=0 NormalY=0 NormalZ=1 AngleXU=0 Radius=1
    g30: LineSegment StartX=-17.5025 StartY=-5 StartZ=0 EndX=-18.3685 EndY=-5.5 EndZ=0
    g31: LineSegment StartX=-18.3685 StartY=-5.5 StartZ=0 EndX=-18.3685 EndY=-6.5 EndZ=0
    g32: LineSegment StartX=-18.3685 StartY=-6.5 StartZ=0 EndX=-17.5025 EndY=-7 EndZ=0
    g33: LineSegment StartX=-17.5025 StartY=-7 StartZ=0 EndX=-16.6365 EndY=-6.5 EndZ=0
    g34: LineSegment StartX=-16.6365 StartY=-6.5 StartZ=0 EndX=-16.6365 EndY=-5.5 EndZ=0
    g35: LineSegment StartX=-16.6365 StartY=-5.5 StartZ=0 EndX=-17.5025 EndY=-5 EndZ=0
    g36: Circle CenterX=-17.5025 CenterY=-6 CenterZ=0 NormalX=0 NormalY=0 NormalZ=1 AngleXU=0 Radius=1
  constraints (88):
    c: Coincident(g2,g3)
    c: Coincident(g3,g0)
    c: Horizontal(g0)
    c: Horizontal(g2)
    c: Vertical(g1)
    c: Vertical(g3)
    c: Distance(g-1,g2) = 6
    c: Distance(g-1,g0) = 6
    c: Distance(g0,g-2) = 7.5
    c: Distance(g-1,g1) = 7.5
    c: Coincident(g4,g2)
    c: Coincident(g5,g0)
    c: Diameter(g4) = 2
    c: Diameter(g5) = 2
    c: Coincident(g6,g7)
    c: Coincident(g7,g8)
    c: Coincident(g8,g9)
    c: Coincident(g9,g10)
    c: Coincident(g10,g11)
    c: Coincident(g11,g6)
    c: Equal(g6, g7-g11) x5
    c: PointOnObject(g6,g12)
    c: PointOnObject(g7,g12)
    c: PointOnObject(g8,g12)
    c: PointOnObject(g9,g12)
    c: PointOnObject(g10,g12)
    c: PointOnObject(g11,g12)
    c: Coincident(g12,g2)
    c: PointOnObject(g11,g4)
    c: Coincident(g13,g14)
    c: Coincident(g14,g15)
    c: Coincident(g15,g16)
    c: Coincident(g16,g17)
    c: Coincident(g17,g18)
    c: Coincident(g18,g13)
    c: Equal(g13, g14-g18) x5
    c: PointOnObject(g13,g19)
    c: PointOnObject(g14,g19)
    c: PointOnObject(g15,g19)
    c: PointOnObject(g16,g19)
    c: PointOnObject(g17,g19)
    c: PointOnObject(g18,g19)
    c: Coincident(g19,g0)
    c: PointOnObject(g18,g5)
    c: Perpendicular(g3,g11)
    c: Perpendicular(g3,g14)
    c: Coincident(g1,g0)
    c: Coincident(g1,g2)
    c: Coincident(g20,g0)
    c: Horizontal(g20)
    c: Vertical(g21)
    c: Coincident(g22,g2)
    c: Horizontal(g22)
    c: Distance(g-1,g21) = 17.5025
    c: Coincident(g20,g21)
    c: Coincident(g21,g22)
    c: Coincident(g23,g24)
    c: Coincident(g24,g25)
    c: Coincident(g25,g26)
    c: Coincident(g26,g27)
    c: Coincident(g27,g28)
    c: Coincident(g28,g23)
    c: Equal(g23, g24-g28) x5
    c: PointOnObject(g23,g29)
    c: PointOnObject(g24,g29)
    c: PointOnObject(g25,g29)
    c: PointOnObject(g26,g29)
    c: PointOnObject(g27,g29)
    c: PointOnObject(g28,g29)
    c: Coincident(g29,g20)
    c: PointOnObject(g28,g21)
    c: Diameter(g29) = 2
    c: Coincident(g30,g31)
    c: Coincident(g31,g32)
    c: Coincident(g32,g33)
    c: Coincident(g33,g34)
    c: Coincident(g34,g35)
    c: Coincident(g35,g30)
    c: Equal(g30, g31-g35) x5
    c: PointOnObject(g30,g36)
    c: PointOnObject(g31,g36)
    c: PointOnObject(g32,g36)
    c: PointOnObject(g33,g36)
    c: PointOnObject(g34,g36)
    c: PointOnObject(g35,g36)
    c: Coincident(g36,g21)
    c: PointOnObject(g35,g21)
    c: Diameter(g36) = 2
FEATURE [Sketcher::SketchObject] Sketch014
  FullyConstrained = true
  MapMode = 5
  Placement = pos=(0,0,0) rot=(1,0,0;1.5708rad)
  Support = -> [XZ_Plane001]
  expr: Constraints[1] = Spreadsheet.ball_z
  expr: Constraints[2] = Spreadsheet.radius + Spreadsheet.bearing_radius
  expr: Constraints[4] = Spreadsheet.bearing_radius * 2 + 0.01
  expr: Constraints[5] = Spreadsheet.bearing_a1
  sketch-geometry (2):
    g0: LineSegment StartX=0 StartY=9.8 StartZ=0 EndX=-10.8088 EndY=13.7341 EndZ=0
    g1: Circle CenterX=-10.8088 CenterY=13.7341 CenterZ=0 NormalX=0 NormalY=0 NormalZ=1 AngleXU=0 Radius=2.005
  constraints (6):
    c: PointOnObject(g0,g-2)
    c: Distance(g0,g-1) = 9.8
    c: Distance(g0) = 11.5025
    c: Coincident(g1,g0)
    c: Diameter(g1) = 4.01
    c: Angle(g0,g-2) = 1.91986
FEATURE [PartDesign::Pad] Pad002
  BaseFeature = -> Sphere001
  Direction = (0,-1,-2e-16)
  Length = 2
  Length2 = 10
  Midplane = true
  Placement = pos=(0,0,9.8) rot=(0,0,1;0rad)
  Profile = -> Sketch014
  ReferenceAxis = -> Sketch014 [N_Axis]
  Type = 0
  expr: Length = Spreadsheet.bearing_t
FEATURE [Sketcher::SketchObject] Sketch015
  FullyConstrained = false
  MapMode = 5
  Placement = pos=(0,0,0) rot=(1,0,0;1.5708rad)
  Support = -> [XZ_Plane001]
  expr: Constraints[1] = Spreadsheet.ball_z
  expr: Constraints[2] = Spreadsheet.bearing_a1
  expr: Constraints[3] = Spreadsheet.bearing_a2
  expr: Constraints[5] = (Spreadsheet.bearing_a1 + Spreadsheet.bearing_a2) / 2
  sketch-geometry (3):
    g0: LineSegment StartX=0 StartY=9.8 StartZ=0 EndX=-8.30448 EndY=12.8226 EndZ=0
    g1: LineSegment StartX=0 StartY=13 StartZ=0 EndX=3.2963 EndY=7.29064 EndZ=0
    g2: LineSegment StartX=9.17198 StartY=20.7307 StartZ=0 EndX=-4.85821 EndY=4.01021 EndZ=0
  constraints (6):
    c: PointOnObject(g0,g-2)
    c: Distance(g0,g-1) = 9.8
    c: Angle(g0,g-2) = 1.91986
    c: Angle(g-2,g1) = 0.523599
    c: PointOnObject(g0,g2)
    c: Angle(g0,g2) = 1.22173
FEATURE [PartDesign::Line] DatumLine001
  AttacherType = Attacher::AttachEngineLine
  Length = 20
  MapMode = 29
  Placement = pos=(-4.82556,-9e-16,4.04912) rot=(-0.684791,0.684791,0.249244;3.63013rad)
  ResizeMode = 0
  Support = -> [Sketch015]
FEATURE [PartDesign::PolarPattern] PolarPattern001
  Angle = 360
  Axis = -> DatumLine001
  BaseFeature = -> Pad002
  Occurrences = 3
  Originals = -> [Pad002]
  Placement = pos=(0,0,9.8) rot=(0,0,1;0rad)
FEATURE [PartDesign::Body] Body001  label="ボールと支持ベアリング"
  Group = -> [Sphere001,Sketch014,Pad002,Sketch015,DatumLine001,PolarPattern001]
  Origin = -> Origin001
  Tip = -> PolarPattern001
FEATURE [PartDesign::Chamfer] Chamfer
  Angle = 45
  Base = -> Pocket009 [Edge93,Edge184,Edge161,Edge94,Edge186,Edge187,Edge160]
  BaseFeature = -> Pocket009
  ChamferType = 0
  FlipDirection = false
  Placement = pos=(0,0,9.8) rot=(0,0,1;0rad)
  Size = 1
  Size2 = 1
  SupportTransform = false
  UseAllEdges = false
FEATURE [PartDesign::Pocket] Pocket010  label="固定穴"
  BaseFeature = -> Chamfer
  Direction = (0,0,-1)
  Length = 6
  Length2 = 5
  Placement = pos=(0,0,9.8) rot=(0,0,1;0rad)
  Profile = -> Sketch013
  ReferenceAxis = -> Sketch013 [N_Axis]
  Reversed = true
  Type = 0
FEATURE [PartDesign::Body] Body
  Group = -> [Sketch,Pad,Sketch009,Pocket006,Sphere,Sketch001,Pocket,Sketch002,Pocket001,Sketch006,DatumLine,DatumPoint,DatumPlane,Sketch003,Sketch010,Pocket007,Pocket002,Sketch004,Pad001,Sketch005,Pocket003,PolarPattern,Mirrored,Sketch007,Pocket004,Sketch008,Pocket005,Sketch011,Pocket008,Sketch012,Pocket009,Sketch013,Chamfer,Pocket010]
  Origin = -> Origin
  Tip = -> Pocket010
